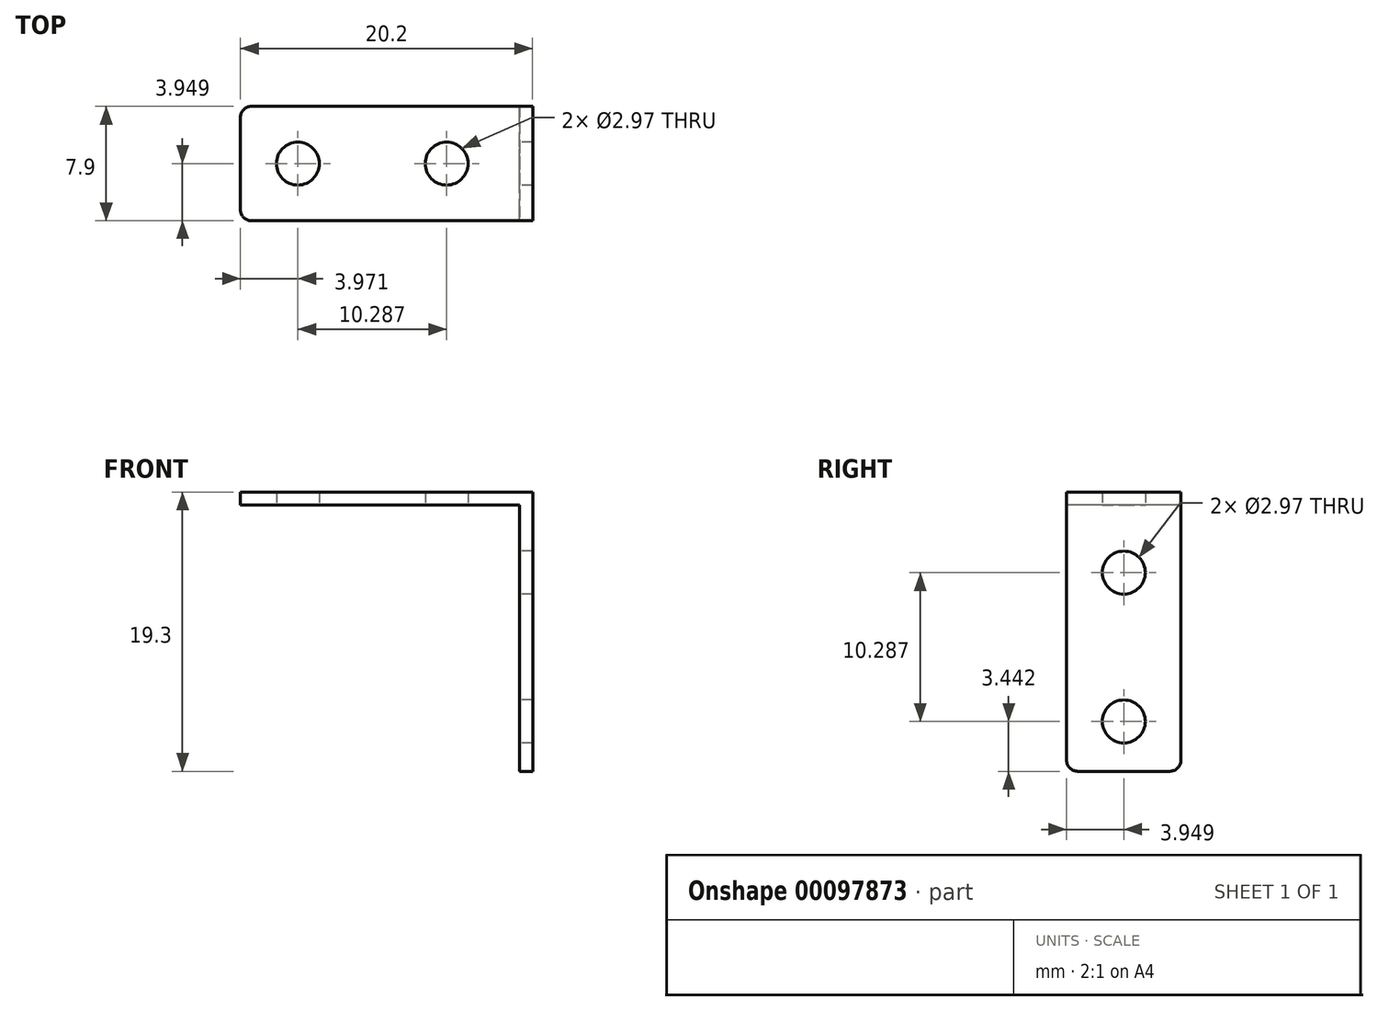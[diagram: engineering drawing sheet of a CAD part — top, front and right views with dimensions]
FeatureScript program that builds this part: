
annotation { "Feature Type Name" : "Feature", "Feature Type Description" : "" }
export const myFeature = defineFeature(function(context is Context, id is Id, definition is map)
    precondition{}
    {
        {
            var Q0;
            Q0=qCreatedBy(makeId("Top.planeOp"),FACE);
            var sketch = newSketch(context, id + "F0", { "sketchPlane" : qUnion([Q0])});
            skLineSegment(sketch, "E0.bottom", {"start": v(-58.17, -9.46) * mm, "end": v(-38.87, -9.46) * mm});
            skLineSegment(sketch, "E0.top", {"start": v(-58.17, -17.36) * mm, "end": v(-38.87, -17.36) * mm});
            skLineSegment(sketch, "E0.left", {"start": v(-58.17, -9.46) * mm, "end": v(-58.17, -17.36) * mm});
            skLineSegment(sketch, "E0.right", {"start": v(-38.87, -9.46) * mm, "end": v(-38.87, -17.36) * mm});
            skSolve(sketch);
        }
        {
            var Q0;
            Q0=qSketchRegion(id+"F0",true);
            extrude(context, id + "F1", {"entities" : qUnion([Q0]), "depth" : 0.91 * mm});
        }
        {
            var Q0;
            Q0=makeQuery(id+"F1.opExtrude","CAP_FACE",FACE,{"disambiguationData":[OSD([sQuery(id+"F0.wireOp",EDGE,"E0.bottom"),sQuery(id+"F0.wireOp",EDGE,"E0.top"),sQuery(id+"F0.wireOp",EDGE,"E0.left"),sQuery(id+"F0.wireOp",EDGE,"E0.right")])],"isStart":true});
            var sketch = newSketch(context, id + "F2", { "sketchPlane" : qUnion([Q0])});
            skCircle(sketch, "E1", {"center": v(-54.2, 13.41) * mm, "radius": 1.49 * mm});
            skCircle(sketch, "E2.1.0.0", {"center": v(-43.91, 13.41) * mm, "radius": 1.49 * mm});
            skLineSegment(sketch, "E2.direction1", {"start": v(-54.2, 13.41) * mm, "end": v(-43.91, 13.41) * mm, "construction": true});
            skLineSegment(sketch, "E3", {"start": v(-43.91, 17.36) * mm, "end": v(-43.91, 9.46) * mm, "construction": true});
            skSolve(sketch);
        }
        {
            var Q0;
            Q0=qSketchRegion(id+"F2",true);
            extrude(context, id + "F3", {"entities" : qUnion([Q0]), "operationType" : NewBodyOperationType.REMOVE, "oppositeDirection" : true, "depth" : 25.4 * mm});
        }
        {
            var Q0;
            Q0=makeQuery(id+"F1.opExtrude","SWEPT_FACE",FACE,{"disambiguationData":[OSD([sQuery(id+"F0.wireOp",EDGE,"E0.right")])]});
            var sketch = newSketch(context, id + "F4", { "sketchPlane" : qUnion([Q0])});
            skLineSegment(sketch, "E4.bottom", {"start": v(-17.36, 0.91) * mm, "end": v(-9.46, 0.91) * mm});
            skLineSegment(sketch, "E4.top", {"start": v(-17.36, -18.39) * mm, "end": v(-9.46, -18.39) * mm});
            skLineSegment(sketch, "E4.left", {"start": v(-17.36, 0.91) * mm, "end": v(-17.36, -18.39) * mm});
            skLineSegment(sketch, "E4.right", {"start": v(-9.46, 0.91) * mm, "end": v(-9.46, -18.39) * mm});
            skSolve(sketch);
        }
        {
            var Q0;
            Q0=qSketchRegion(id+"F4",true);
            extrude(context, id + "F5", {"entities" : qUnion([Q0]), "operationType" : NewBodyOperationType.ADD, "depth" : 0.9 * mm});
        }
        {
            var Q0;
            Q0=makeQuery(id+"F5.opExtrude","CAP_FACE",FACE,{"disambiguationData":[OSD([sQuery(id+"F4.wireOp",EDGE,"E4.bottom"),sQuery(id+"F4.wireOp",EDGE,"E4.top"),sQuery(id+"F4.wireOp",EDGE,"E4.left"),sQuery(id+"F4.wireOp",EDGE,"E4.right")])],"isStart":true});
            var sketch = newSketch(context, id + "F6", { "sketchPlane" : qUnion([Q0])});
            skCircle(sketch, "E5", {"center": v(13.41, -4.66) * mm, "radius": 1.49 * mm});
            skLineSegment(sketch, "E6", {"start": v(17.36, -4.66) * mm, "end": v(9.46, -4.66) * mm, "construction": true});
            skCircle(sketch, "E7.0.1.0", {"center": v(13.41, -14.95) * mm, "radius": 1.49 * mm});
            skLineSegment(sketch, "E7.direction2", {"start": v(13.41, -4.66) * mm, "end": v(13.41, -14.95) * mm, "construction": true});
            skSolve(sketch);
        }
        {
            var Q0;
            Q0=qSketchRegion(id+"F6",true);
            extrude(context, id + "F7", {"entities" : qUnion([Q0]), "operationType" : NewBodyOperationType.REMOVE, "oppositeDirection" : true, "depth" : 25.4 * mm});
        }
        {
            var Q0;
            Q0=makeQuery(id+"F1.opExtrude","SWEPT_EDGE",EDGE,{"disambiguationData":[OSD([sQuery(id+"F0.wireOp",EDGE,"E0.top"),sQuery(id+"F0.wireOp",EDGE,"E0.left")])]});
            var Q1;
            Q1=makeQuery(id+"F1.opExtrude","SWEPT_EDGE",EDGE,{"disambiguationData":[OSD([sQuery(id+"F0.wireOp",EDGE,"E0.bottom"),sQuery(id+"F0.wireOp",EDGE,"E0.left")])]});
            var Q2;
            Q2=makeQuery(id+"F5.opExtrude","SWEPT_EDGE",EDGE,{"disambiguationData":[OSD([sQuery(id+"F4.wireOp",EDGE,"E4.top"),sQuery(id+"F4.wireOp",EDGE,"E4.left")])]});
            var Q3;
            Q3=makeQuery(id+"F5.opExtrude","SWEPT_EDGE",EDGE,{"disambiguationData":[OSD([sQuery(id+"F4.wireOp",EDGE,"E4.top"),sQuery(id+"F4.wireOp",EDGE,"E4.right")])]});
            fillet(context, id + "F8", {"entities" : qUnion([Q0, Q1, Q2, Q3]), "radius" : 0.76 * mm, "tangentPropagation" : true, "allowEdgeOverflow" : false});
        }
    });
